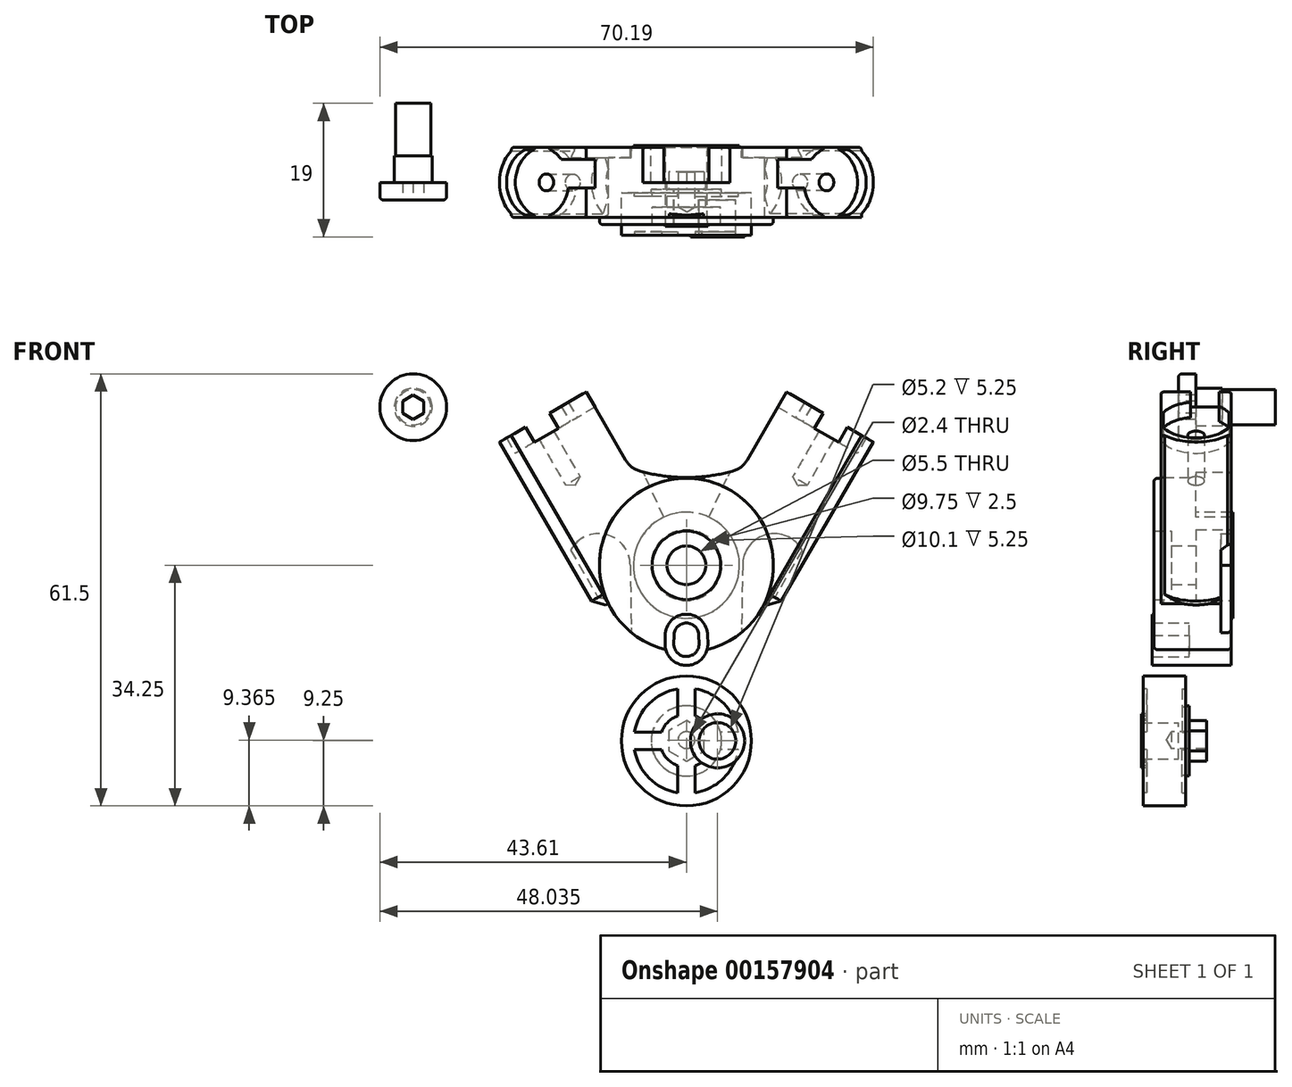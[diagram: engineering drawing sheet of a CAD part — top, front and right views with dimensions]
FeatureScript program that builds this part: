
annotation { "Feature Type Name" : "Feature", "Feature Type Description" : "" }
export const myFeature = defineFeature(function(context is Context, id is Id, definition is map)
    precondition{}
    {
        {
            var Q0;
            Q0=qCreatedBy(makeId("Front.planeOp"),FACE);
            var sketch = newSketch(context, id + "F0", { "sketchPlane" : qUnion([Q0])});
            skPoint(sketch, "E0.orphan", {"position": v(0, -22.5) * mm});
            skLineSegment(sketch, "E1", {"start": v(13, 0) * mm, "end": v(23.68, -6.17) * mm});
            skLineSegment(sketch, "E2.MirrorCS", {"start": v(-13, 0) * mm, "end": v(-23.68, -6.17) * mm});
            skLineSegment(sketch, "E3", {"start": v(-13, 0) * mm, "end": v(-8.66, -7.5) * mm});
            skLineSegment(sketch, "E4", {"start": v(13, 0) * mm, "end": v(8.66, -7.5) * mm});
            skLineSegment(sketch, "E5.MirrorCS", {"start": v(-11.11, -27.95) * mm, "end": v(-23.68, -6.17) * mm});
            skArc(sketch, "E6", {"start": v(-6.55, -9.13) * mm, "mid": v(0, -10) * mm, "end": v(6.55, -9.13) * mm});
            skPoint(sketch, "E7.visualSharp", {"position": v(-7.97, -8.7) * mm});
            skArc(sketch, "E7.filletArc", {"start": v(-8.66, -7.5) * mm, "mid": v(-7.76, -8.52) * mm, "end": v(-6.55, -9.13) * mm});
            skPoint(sketch, "E8.visualSharp", {"position": v(7.97, -8.7) * mm});
            skArc(sketch, "E8.filletArc", {"start": v(6.55, -9.13) * mm, "mid": v(7.76, -8.52) * mm, "end": v(8.66, -7.5) * mm});
            skArc(sketch, "E9", {"start": v(-11.11, -27.95) * mm, "mid": v(0, -34.87) * mm, "end": v(11.11, -27.95) * mm});
            skLineSegment(sketch, "E10", {"start": v(23.68, -6.17) * mm, "end": v(11.11, -27.95) * mm});
            skLineSegment(sketch, "E11", {"start": v(0, -22.5) * mm, "end": v(0, -33.7) * mm});
            skCircle(sketch, "E12", {"center": v(0, -33.7) * mm, "radius": 1.8 * mm});
            skCircle(sketch, "E13.0", {"center": v(0, -33.7) * mm, "radius": 3.05 * mm});
            skSolve(sketch);
        }
        {
            var Q0;
            Q0 = qSketchRegion(id + "F0", true);
            var Q1;
            {var subQ0=sQuery(id+"F0.wireOp",EDGE,"E12");var subQ1=sQuery(id+"F0.wireOp",EDGE,"E9");var subQ2=makeQuery(id+"F0.imprint","INTERSECT",VERTEX,{"disambiguationData":[OD(0.0)],"derivedFrom":[subQ1,subQ0]});Q1=makeQuery(id+"F0.imprint","IMPRINT",FACE,{"disambiguationData":[TD([[makeQuery(id+"F0.imprint","IMPRINT",EDGE,{"disambiguationData":[TD([[subQ2,-1.0]])],"derivedFrom":subQ1}),1.0]])]});}
            var Q2;
            {var subQ0=sQuery(id+"F0.wireOp",EDGE,"E12");var subQ1=sQuery(id+"F0.wireOp",EDGE,"E9");var subQ2=makeQuery(id+"F0.imprint","INTERSECT",VERTEX,{"disambiguationData":[OD(0.0)],"derivedFrom":[subQ1,subQ0]});Q2=makeQuery(id+"F0.imprint","IMPRINT",FACE,{"disambiguationData":[TD([[makeQuery(id+"F0.imprint","IMPRINT",EDGE,{"disambiguationData":[TD([[subQ2,-1.0]])],"derivedFrom":subQ1}),-1.0]])]});}
            extrude(context, id + "F1", {"entities" : qUnion([Q0, Q1, Q2]), "depth" : 10 * mm, "symmetric" : true});
        }
        {
            var Q0;
            Q0=makeQuery(id+"F1.opExtrude","SWEPT_FACE",FACE,{"disambiguationData":[OSD([sQuery(id+"F0.wireOp",EDGE,"E2.MirrorCS")])]});
            var sketch = newSketch(context, id + "F2", { "sketchPlane" : qUnion([Q0])});
            skCircle(sketch, "E14", {"center": v(-19.25, 0) * mm, "radius": 2.06 * mm});
            skSolve(sketch);
        }
        {
            var Q0;
            Q0=makeQuery(id+"F1.opExtrude","SWEPT_FACE",FACE,{"disambiguationData":[OSD([sQuery(id+"F0.wireOp",EDGE,"E1")])]});
            var sketch = newSketch(context, id + "F3", { "sketchPlane" : qUnion([Q0])});
            skPoint(sketch, "E15.orphan", {"position": v(38.32, 0.04) * mm});
            skPoint(sketch, "E16.orphan", {"position": v(-25.5, -0.17) * mm});
            skCircle(sketch, "E17", {"center": v(19.25, 0) * mm, "radius": 1.81 * mm});
            skSolve(sketch);
        }
        {
            var Q0;
            Q0=sQuery(id+"F2.wireOp",VERTEX,"E14.center");
            var Q1;
            Q1=makeQuery(id+"F1.opExtrude","SWEPT_BODY",BODY,{"disambiguationData":[OSD([sQuery(id+"F0.wireOp",EDGE,"rzOBaQMi-jGq5-lYb1-NnJw-oWnWe92DnjdN"),sQuery(id+"F0.wireOp",EDGE,"d8c17911-49cf-4aa5-88f4-c349b0b964bf0.MirrorCS"),sQuery(id+"F0.wireOp",EDGE,"bd97ef09-3599-47c6-b334-9f93c697f875.0"),sQuery(id+"F0.wireOp",EDGE,"KOXjZ0GF-IRyi-H7XW-LbBs-y6uAzEbRzkAs"),sQuery(id+"F0.wireOp",EDGE,"1ec44e12-bc36-4326-98cc-bccb7114c2df.trimOffspring"),sQuery(id+"F0.wireOp",EDGE,"hHBrl5i6-ZnJ3-XNhw-2FA3-8lGi2psnKHFM"),sQuery(id+"F0.wireOp",EDGE,"iY468xlu-Grwu-7jGD-cPJo-sm8Mluo7pk8S"),sQuery(id+"F0.wireOp",EDGE,"xgCmaLVG-ohjl-r4Ya-hG9N-RDTWFdN91myL")])]});
            var Q2;
            Q2=makeQuery(id+"F1.opExtrude","SWEPT_BODY",BODY,{"disambiguationData":[OSD([sQuery(id+"F0.wireOp",EDGE,"rfpI1UyY-z8rJ-t16R-cCYN-fS1l7B0uCpWs"),sQuery(id+"F0.wireOp",EDGE,"E1"),sQuery(id+"F0.wireOp",EDGE,"E2.MirrorCS"),sQuery(id+"F0.wireOp",EDGE,"E3"),sQuery(id+"F0.wireOp",EDGE,"E4"),sQuery(id+"F0.wireOp",EDGE,"lFJJ6whO-Wg9J-KwqN-AuY0-SqxSfbDXyOEt"),sQuery(id+"F0.wireOp",EDGE,"E5.MirrorCS"),sQuery(id+"F0.wireOp",EDGE,"E6"),sQuery(id+"F0.wireOp",EDGE,"E7.filletArc"),sQuery(id+"F0.wireOp",EDGE,"E8.filletArc")])]});
            hole(context, id + "F4", {"style" : HoleStyle.SIMPLE, "endStyle" : HoleEndStyle.BLIND, "standardTappedOrClearance" : lookupTablePath({ "standard" : "ISO", "engagement" : "75%", "pitch" : "0.6 mm", "size" : "M3", "type" : "Tapped" }), "standardBlindInLast" : lookupTablePath({ "standard" : "ISO", "engagement" : "75%", "pitch" : "0.6 mm", "size" : "M3", "type" : "Tapped" }), "holeDiameter" : 2.4 * mm, "holeDepth" : 7.5 * mm, "locations" : qUnion([Q0]), "scope" : qUnion([Q1, Q2]), "startStyle" : HoleStartStyle.SKETCH});
        }
        {
            var Q0;
            Q0=sQuery(id+"F3.wireOp",VERTEX,"E17.center");
            var Q1;
            Q1=makeQuery(id+"F1.opExtrude","SWEPT_BODY",BODY,{"disambiguationData":[OSD([sQuery(id+"F0.wireOp",EDGE,"rfpI1UyY-z8rJ-t16R-cCYN-fS1l7B0uCpWs"),sQuery(id+"F0.wireOp",EDGE,"E1"),sQuery(id+"F0.wireOp",EDGE,"E2.MirrorCS"),sQuery(id+"F0.wireOp",EDGE,"E3"),sQuery(id+"F0.wireOp",EDGE,"E4"),sQuery(id+"F0.wireOp",EDGE,"lFJJ6whO-Wg9J-KwqN-AuY0-SqxSfbDXyOEt"),sQuery(id+"F0.wireOp",EDGE,"E5.MirrorCS"),sQuery(id+"F0.wireOp",EDGE,"E6"),sQuery(id+"F0.wireOp",EDGE,"E7.filletArc"),sQuery(id+"F0.wireOp",EDGE,"E8.filletArc")])]});
            hole(context, id + "F5", {"style" : HoleStyle.SIMPLE, "endStyle" : HoleEndStyle.BLIND, "standardTappedOrClearance" : lookupTablePath({ "standard" : "ISO", "engagement" : "75%", "pitch" : "0.6 mm", "size" : "M3", "type" : "Tapped" }), "standardBlindInLast" : lookupTablePath({ "standard" : "ISO", "engagement" : "75%", "pitch" : "0.6 mm", "size" : "M3", "type" : "Tapped" }), "holeDiameter" : 2.4 * mm, "holeDepth" : 7.5 * mm, "locations" : qUnion([Q0]), "scope" : qUnion([Q1]), "startStyle" : HoleStartStyle.SKETCH});
        }
        {
            var Q0;
            Q0=makeQuery(id+"F1.opExtrude","CAP_FACE",FACE,{"disambiguationData":[OSD([sQuery(id+"F0.wireOp",EDGE,"rfpI1UyY-z8rJ-t16R-cCYN-fS1l7B0uCpWs"),sQuery(id+"F0.wireOp",EDGE,"E1"),sQuery(id+"F0.wireOp",EDGE,"E2.MirrorCS"),sQuery(id+"F0.wireOp",EDGE,"E3"),sQuery(id+"F0.wireOp",EDGE,"E4"),sQuery(id+"F0.wireOp",EDGE,"lFJJ6whO-Wg9J-KwqN-AuY0-SqxSfbDXyOEt"),sQuery(id+"F0.wireOp",EDGE,"E5.MirrorCS"),sQuery(id+"F0.wireOp",EDGE,"E6"),sQuery(id+"F0.wireOp",EDGE,"E7.filletArc"),sQuery(id+"F0.wireOp",EDGE,"E8.filletArc")])],"isStart":false});
            var sketch = newSketch(context, id + "F6", { "sketchPlane" : qUnion([Q0])});
            skCircle(sketch, "E18", {"center": v(0, -22.5) * mm, "radius": 12.37 * mm});
            skCircle(sketch, "E19.0", {"center": v(0, -33.7) * mm, "radius": 3.05 * mm});
            skSolve(sketch);
        }
        {
            var Q0;
            Q0 = qSketchRegion(id + "F6", true);
            extrude(context, id + "F7", {"entities" : qUnion([Q0]), "operationType" : NewBodyOperationType.ADD, "depth" : 1 * mm});
        }
        {
            var Q0;
            Q0=makeQuery(id+"F7.opExtrude","CAP_FACE",FACE,{"disambiguationData":[OSD([sQuery(id+"F6.wireOp",EDGE,"E18")])],"isStart":false});
            var sketch = newSketch(context, id + "F8", { "sketchPlane" : qUnion([Q0])});
            skPoint(sketch, "E20", {"position": v(0, -22.5) * mm});
            skSolve(sketch);
        }
        {
            var Q0;
            Q0=sQuery(id+"F8.wireOp",VERTEX,"E20");
            var Q1;
            Q1=makeQuery(id+"F1.opExtrude","SWEPT_BODY",BODY,{"disambiguationData":[OSD([sQuery(id+"F0.wireOp",EDGE,"rfpI1UyY-z8rJ-t16R-cCYN-fS1l7B0uCpWs"),sQuery(id+"F0.wireOp",EDGE,"E1"),sQuery(id+"F0.wireOp",EDGE,"E2.MirrorCS"),sQuery(id+"F0.wireOp",EDGE,"E3"),sQuery(id+"F0.wireOp",EDGE,"E4"),sQuery(id+"F0.wireOp",EDGE,"lFJJ6whO-Wg9J-KwqN-AuY0-SqxSfbDXyOEt"),sQuery(id+"F0.wireOp",EDGE,"E5.MirrorCS"),sQuery(id+"F0.wireOp",EDGE,"E6"),sQuery(id+"F0.wireOp",EDGE,"E7.filletArc"),sQuery(id+"F0.wireOp",EDGE,"E8.filletArc")])]});
            hole(context, id + "F9", {"style" : HoleStyle.C_BORE, "endStyle" : HoleEndStyle.THROUGH, "holeDiameter" : 5.5 * mm, "cBoreDiameter" : 9.75 * mm, "cBoreDepth" : 2.5 * mm, "locations" : qUnion([Q0]), "scope" : qUnion([Q1]), "isTappedThrough" : true, "startStyle" : HoleStartStyle.SKETCH});
        }
        {
            var Q0;
            Q0=makeQuery(id+"F1.opExtrude","SWEPT_FACE",FACE,{"disambiguationData":[OSD([sQuery(id+"F0.wireOp",EDGE,"E2.MirrorCS")])]});
            var sketch = newSketch(context, id + "F10", { "sketchPlane" : qUnion([Q0])});
            skLineSegment(sketch, "E21.0", {"start": v(-23.6, -4.5) * mm, "end": v(-23.6, 4.5) * mm});
            skArc(sketch, "E22", {"start": v(-23.6, 4.5) * mm, "mid": v(-25.5, 0) * mm, "end": v(-23.6, -4.5) * mm});
            skPoint(sketch, "E23.orphan", {"position": v(-23.6, -5) * mm});
            skPoint(sketch, "E24.orphan", {"position": v(-23.6, 5) * mm});
            skSolve(sketch);
        }
        {
            var Q0;
            Q0=makeQuery(id+"FtnkNii1LFd0vET_1.boolean.opBoolean","MERGE",FACE,{"derivedFrom":[makeQuery(id+"F1.opExtrude","SWEPT_FACE",FACE,{"disambiguationData":[OSD([sQuery(id+"F0.wireOp",EDGE,"E2.MirrorCS")])]}),makeQuery(id+"FtnkNii1LFd0vET_1.opSweep","CAP_FACE",FACE,{"disambiguationData":[OSD([sQuery(id+"F0.wireOp",VERTEX,"E5.MirrorCS.end"),sQuery(id+"F10.wireOp",EDGE,"03euvT1h-kaf3-RjWf-RbOj-bPACf7aRniEZ"),sQuery(id+"F10.wireOp",EDGE,"Vvxw1KTZ-P8wy-A8oR-Xbjp-Nn9TtI1LRVrt")])],"isStart":true})]});
            var sketch = newSketch(context, id + "F11", { "sketchPlane" : qUnion([Q0])});
            skArc(sketch, "E25", {"start": v(-15.36, 3.3) * mm, "mid": v(-16.22, 4.1) * mm, "end": v(-17.25, 4.7) * mm});
            skLineSegment(sketch, "E26", {"start": v(-23.6, 5) * mm, "end": v(-21.25, 5) * mm});
            skLineSegment(sketch, "E27", {"start": v(-11.25, 5) * mm, "end": v(-11.25, 3.3) * mm});
            skLineSegment(sketch, "E28", {"start": v(-11.25, -5) * mm, "end": v(-17.25, -5) * mm});
            skLineSegment(sketch, "E29", {"start": v(-11.25, 3.3) * mm, "end": v(-15.36, 3.3) * mm});
            skLineSegment(sketch, "E30", {"start": v(-11.25, -0.8) * mm, "end": v(-14.21, -0.8) * mm});
            skLineSegment(sketch, "E31.trimOffspring", {"start": v(-11.25, -0.8) * mm, "end": v(-11.25, -5) * mm});
            skLineSegment(sketch, "E32", {"start": v(-23.6, 5) * mm, "end": v(-23.6, 4.5) * mm});
            skLineSegment(sketch, "E33.trimOffspring", {"start": v(-23.6, -4.5) * mm, "end": v(-23.6, -5) * mm});
            skArc(sketch, "E34.trimOffspring", {"start": v(-21.25, 4.7) * mm, "mid": v(-24.35, 0) * mm, "end": v(-21.25, -4.7) * mm});
            skArc(sketch, "E35.trimOffspring", {"start": v(-17.25, -4.7) * mm, "mid": v(-15.23, -3.14) * mm, "end": v(-14.21, -0.8) * mm});
            skLineSegment(sketch, "E36", {"start": v(-21.25, 5) * mm, "end": v(-21.25, 4.7) * mm});
            skLineSegment(sketch, "E37.0", {"start": v(-17.25, 5) * mm, "end": v(-17.25, 4.7) * mm});
            skLineSegment(sketch, "E38.trimOffspring", {"start": v(-17.25, 5) * mm, "end": v(-11.25, 5) * mm});
            skLineSegment(sketch, "E39.trimOffspring", {"start": v(-17.25, -4.7) * mm, "end": v(-17.25, -5) * mm});
            skLineSegment(sketch, "E40.trimOffspring", {"start": v(-18.25, -5) * mm, "end": v(-20.25, -5) * mm});
            skLineSegment(sketch, "E41.trimOffspring", {"start": v(-21.25, -5) * mm, "end": v(-23.6, -5) * mm});
            skLineSegment(sketch, "E42.trimOffspring", {"start": v(-21.25, -4.7) * mm, "end": v(-21.25, -5) * mm});
            skArc(sketch, "E43", {"start": v(-23.6, 4.5) * mm, "mid": v(-25.5, 0) * mm, "end": v(-23.6, -4.5) * mm});
            skSolve(sketch);
        }
        {
            var Q0;
            Q0 = qSketchRegion(id + "F11", true);
            extrude(context, id + "F12", {"entities" : qUnion([Q0]), "operationType" : NewBodyOperationType.ADD, "depth" : 2.5 * mm});
        }
        {
            var Q0;
            Q0=makeQuery(id+"FtnkNii1LFd0vET_1.boolean.opBoolean","MERGE",FACE,{"derivedFrom":[makeQuery(id+"F1.opExtrude","SWEPT_FACE",FACE,{"disambiguationData":[OSD([sQuery(id+"F0.wireOp",EDGE,"E1")])]}),makeQuery(id+"FtnkNii1LFd0vET_1.opSweep","CAP_FACE",FACE,{"disambiguationData":[OSD([sQuery(id+"F0.wireOp",VERTEX,"lFJJ6whO-Wg9J-KwqN-AuY0-SqxSfbDXyOEt.end"),sQuery(id+"F10.wireOp",EDGE,"03euvT1h-kaf3-RjWf-RbOj-bPACf7aRniEZ"),sQuery(id+"F10.wireOp",EDGE,"Vvxw1KTZ-P8wy-A8oR-Xbjp-Nn9TtI1LRVrt")])],"isStart":false})]});
            var sketch = newSketch(context, id + "F13", { "sketchPlane" : qUnion([Q0])});
            skArc(sketch, "E44", {"start": v(14.21, -0.8) * mm, "mid": v(15.23, -3.14) * mm, "end": v(17.25, -4.7) * mm});
            skLineSegment(sketch, "E45", {"start": v(11.25, -5) * mm, "end": v(11.25, -0.8) * mm});
            skLineSegment(sketch, "E46", {"start": v(11.25, 5) * mm, "end": v(17.25, 5) * mm});
            skLineSegment(sketch, "E47", {"start": v(11.25, -5) * mm, "end": v(17.25, -5) * mm});
            skLineSegment(sketch, "E48", {"start": v(11.25, 3.3) * mm, "end": v(15.36, 3.3) * mm});
            skLineSegment(sketch, "E49", {"start": v(11.25, -0.8) * mm, "end": v(14.21, -0.8) * mm});
            skLineSegment(sketch, "E50.trimOffspring", {"start": v(11.25, 3.3) * mm, "end": v(11.25, 5) * mm});
            skArc(sketch, "E51", {"start": v(23.6, -4.5) * mm, "mid": v(25.5, 0) * mm, "end": v(23.6, 4.5) * mm});
            skLineSegment(sketch, "E52", {"start": v(21.25, -5) * mm, "end": v(21.25, -4.7) * mm});
            skLineSegment(sketch, "E53.0", {"start": v(17.25, -5) * mm, "end": v(17.25, -4.7) * mm});
            skLineSegment(sketch, "E54.trimOffspring", {"start": v(21.25, 4.7) * mm, "end": v(21.25, 5) * mm});
            skLineSegment(sketch, "E55.trimOffspring", {"start": v(17.25, 4.7) * mm, "end": v(17.25, 5) * mm});
            skArc(sketch, "E56.trimOffspring", {"start": v(17.25, 4.7) * mm, "mid": v(16.22, 4.1) * mm, "end": v(15.36, 3.3) * mm});
            skArc(sketch, "E57.trimOffspring", {"start": v(21.25, -4.7) * mm, "mid": v(24.35, 0) * mm, "end": v(21.25, 4.7) * mm});
            skLineSegment(sketch, "E58", {"start": v(21.25, 5) * mm, "end": v(23.6, 5) * mm});
            skLineSegment(sketch, "E59", {"start": v(21.25, -5) * mm, "end": v(23.6, -5) * mm});
            skLineSegment(sketch, "E60", {"start": v(23.6, -5) * mm, "end": v(23.6, -4.5) * mm});
            skLineSegment(sketch, "E61", {"start": v(23.6, 4.5) * mm, "end": v(23.6, 5) * mm});
            skSolve(sketch);
        }
        {
            var Q0;
            Q0 = qSketchRegion(id + "F13", true);
            extrude(context, id + "F14", {"entities" : qUnion([Q0]), "operationType" : NewBodyOperationType.ADD, "depth" : 2.5 * mm});
        }
        {
            var Q0;
            Q0=makeQuery(id+"F10.imprint","IMPRINT",FACE,{"disambiguationData":[TD([[makeQuery(id+"F10.imprint","IMPRINT",EDGE,{"derivedFrom":sQuery(id+"F10.wireOp",EDGE,"E21.0")}),1.0]])]});
            var Q1;
            Q1=sQuery(id+"F0.wireOp",EDGE,"E5.MirrorCS");
            sweep(context, id + "F15", {"operationType" : NewBodyOperationType.ADD, "profiles" : qUnion([Q0]), "path" : qUnion([Q1])});
        }
        {
            var Q0;
            Q0=makeQuery(id+"F14.opExtrude","CAP_FACE",FACE,{"disambiguationData":[OSD([sQuery(id+"F13.wireOp",EDGE,"SZVnfSIk-eu6L-TS2M-XrId-ek2R4wEcxdL5"),sQuery(id+"F13.wireOp",EDGE,"E51"),sQuery(id+"F13.wireOp",EDGE,"d2ed7b6c-8a1b-4353-8f4a-99a53af964f0.trimOffspring"),sQuery(id+"F13.wireOp",EDGE,"E52"),sQuery(id+"F13.wireOp",EDGE,"E54.trimOffspring"),sQuery(id+"F13.wireOp",EDGE,"3468f3f2-538a-47e8-9c80-37b50e91f819.trimOffspring"),sQuery(id+"F13.wireOp",EDGE,"E57.trimOffspring"),sQuery(id+"F13.wireOp",EDGE,"c19fe44b-0edd-49b7-be39-237bb749a952.trimOffspring")])],"isStart":true});
            var sketch = newSketch(context, id + "F16", { "sketchPlane" : qUnion([Q0])});
            skArc(sketch, "E62.0", {"start": v(23.6, 4.5) * mm, "mid": v(25.5, 0) * mm, "end": v(23.6, -4.5) * mm});
            skLineSegment(sketch, "E63", {"start": v(23.6, 4.5) * mm, "end": v(23.6, -4.5) * mm});
            skSolve(sketch);
        }
        {
            var Q0;
            Q0 = qSketchRegion(id + "F16", true);
            var Q1;
            Q1=sQuery(id+"F0.wireOp",EDGE,"E10");
            sweep(context, id + "F17", {"operationType" : NewBodyOperationType.ADD, "profiles" : qUnion([Q0]), "path" : qUnion([Q1])});
        }
        {
            var Q0;
            Q0=makeQuery(id+"F14.boolean.opBoolean","MERGE",FACE,{"derivedFrom":[makeQuery(id+"F12.boolean.opBoolean","MERGE",FACE,{"derivedFrom":[makeQuery(id+"F1.opExtrude","CAP_FACE",FACE,{"disambiguationData":[OSD([sQuery(id+"F0.wireOp",EDGE,"rfpI1UyY-z8rJ-t16R-cCYN-fS1l7B0uCpWs"),sQuery(id+"F0.wireOp",EDGE,"E1"),sQuery(id+"F0.wireOp",EDGE,"E2.MirrorCS"),sQuery(id+"F0.wireOp",EDGE,"E3"),sQuery(id+"F0.wireOp",EDGE,"E4"),sQuery(id+"F0.wireOp",EDGE,"lFJJ6whO-Wg9J-KwqN-AuY0-SqxSfbDXyOEt"),sQuery(id+"F0.wireOp",EDGE,"E5.MirrorCS"),sQuery(id+"F0.wireOp",EDGE,"E6"),sQuery(id+"F0.wireOp",EDGE,"E7.filletArc"),sQuery(id+"F0.wireOp",EDGE,"E8.filletArc"),sQuery(id+"F0.wireOp",EDGE,"Z6kVz02L-fb5r-uzOL-jqxl-xZ710giCbPzr")])],"isStart":true}),makeQuery(id+"F12.opExtrude","SWEPT_FACE",FACE,{"disambiguationData":[OSD([sQuery(id+"F11.wireOp",EDGE,"E26")])]})]}),makeQuery(id+"F14.opExtrude","SWEPT_FACE",FACE,{"disambiguationData":[OSD([sQuery(id+"F13.wireOp",EDGE,"E46")])]})]});
            var sketch = newSketch(context, id + "F18", { "sketchPlane" : qUnion([Q0])});
            skCircle(sketch, "E64", {"center": v(0, -22.5) * mm, "radius": 5.05 * mm});
            skSolve(sketch);
        }
        {
            var Q0;
            Q0 = qSketchRegion(id + "F18", true);
            extrude(context, id + "F19", {"entities" : qUnion([Q0]), "operationType" : NewBodyOperationType.REMOVE, "oppositeDirection" : true, "depth" : 5 * mm});
        }
        {
            var Q0;
            Q0=makeQuery(id+"F15.opSweep","CAP_EDGE",EDGE,{"disambiguationData":[OSD([sQuery(id+"F0.wireOp",VERTEX,"E5.MirrorCS.start"),sQuery(id+"F10.wireOp",EDGE,"E22")])],"isStart":false});
            var Q1;
            Q1=makeQuery(id+"F17.opSweep","CAP_EDGE",EDGE,{"disambiguationData":[OSD([sQuery(id+"F0.wireOp",VERTEX,"E10.end"),sQuery(id+"F16.wireOp",EDGE,"E62.0")])],"isStart":false});
            chamfer(context, id + "F20", {"entities" : qUnion([Q0, Q1]), "width" : 1.5 * mm, "tangentPropagation" : true});
        }
        {
            var Q0;
            Q0=qCreatedBy(makeId("Front.planeOp"),FACE);
            cPlane(context, id + "F21", {"entities" : qUnion([Q0]), "cplaneType" : CPlaneType.OFFSET, "offset" : 1.5 * mm, "width" : 150 * mm, "height" : 150 * mm});
        }
        {
            var Q0;
            Q0=qCreatedBy(id+"F21.planeOp",FACE);
            var sketch = newSketch(context, id + "F22", { "sketchPlane" : qUnion([Q0])});
            skCircle(sketch, "E65", {"center": v(0, -47.5) * mm, "radius": 9.25 * mm});
            skSolve(sketch);
        }
        {
            var Q0;
            Q0 = qSketchRegion(id + "F22", true);
            extrude(context, id + "F23", {"entities" : qUnion([Q0]), "depth" : 6 * mm});
        }
        {
            var Q0;
            Q0=makeQuery(id+"F23.opExtrude","CAP_FACE",FACE,{"disambiguationData":[OSD([sQuery(id+"F22.wireOp",EDGE,"E65")])],"isStart":false});
            var sketch = newSketch(context, id + "F24", { "sketchPlane" : qUnion([Q0])});
            skCircle(sketch, "E66", {"center": v(0, -47.5) * mm, "radius": 4.42 * mm});
            skCircle(sketch, "E67", {"center": v(4.42, -47.5) * mm, "radius": 2.6 * mm});
            skCircle(sketch, "E68.0", {"center": v(4.42, -47.5) * mm, "radius": 3.85 * mm});
            skLineSegment(sketch, "E69", {"start": v(4.42, -47.5) * mm, "end": v(0, -47.5) * mm});
            skSolve(sketch);
        }
        {
            var Q0;
            {var subQ0=sQuery(id+"F24.wireOp",EDGE,"E67");var subQ1=sQuery(id+"F24.wireOp",EDGE,"E66");var subQ2=makeQuery(id+"F24.imprint","INTERSECT",VERTEX,{"disambiguationData":[OD(0.0)],"derivedFrom":[subQ1,subQ0]});Q0=makeQuery(id+"F24.imprint","IMPRINT",FACE,{"disambiguationData":[TD([[makeQuery(id+"F24.imprint","IMPRINT",EDGE,{"disambiguationData":[TD([[subQ2,-1.0]])],"derivedFrom":subQ1}),1.0]])]});}
            var Q1;
            {var subQ0=sQuery(id+"F24.wireOp",EDGE,"E67");var subQ1=sQuery(id+"F24.wireOp",EDGE,"E66");var subQ2=makeQuery(id+"F24.imprint","INTERSECT",VERTEX,{"disambiguationData":[OD(0.0)],"derivedFrom":[subQ1,subQ0]});Q1=makeQuery(id+"F24.imprint","IMPRINT",FACE,{"disambiguationData":[TD([[makeQuery(id+"F24.imprint","IMPRINT",EDGE,{"disambiguationData":[TD([[subQ2,-1.0]])],"derivedFrom":subQ1}),-1.0]])]});}
            var Q2;
            {var subQ0=sQuery(id+"F24.wireOp",EDGE,"E68.0");var subQ1=sQuery(id+"F24.wireOp",EDGE,"E66");var subQ2=makeQuery(id+"F24.imprint","INTERSECT",VERTEX,{"disambiguationData":[OD(1.0)],"derivedFrom":[subQ1,subQ0]});Q2=makeQuery(id+"F24.imprint","IMPRINT",FACE,{"disambiguationData":[TD([[makeQuery(id+"F24.imprint","IMPRINT",EDGE,{"disambiguationData":[TD([[subQ2,-1.0]])],"derivedFrom":subQ1}),-1.0]])]});}
            var Q3;
            {var subQ0=sQuery(id+"F24.wireOp",EDGE,"E68.0");var subQ1=sQuery(id+"F24.wireOp",EDGE,"E66");var subQ2=makeQuery(id+"F24.imprint","INTERSECT",VERTEX,{"disambiguationData":[OD(1.0)],"derivedFrom":[subQ1,subQ0]});Q3=makeQuery(id+"F24.imprint","IMPRINT",FACE,{"disambiguationData":[TD([[makeQuery(id+"F24.imprint","IMPRINT",EDGE,{"disambiguationData":[TD([[subQ2,-1.0]])],"derivedFrom":subQ1}),1.0]])]});}
            extrude(context, id + "F25", {"entities" : qUnion([Q0, Q1, Q2, Q3]), "operationType" : NewBodyOperationType.ADD, "depth" : 0.25 * mm});
        }
        {
            var Q0;
            Q0=makeQuery(id+"F25.boolean.opBoolean","SPLIT",FACE,{"disambiguationData":[TD([makeQuery(id+"F25.opExtrude","SWEPT_FACE",FACE,{"disambiguationData":[OSD([sQuery(id+"F24.wireOp",EDGE,"E67")])]})])],"derivedFrom":makeQuery(id+"F23.opExtrude","CAP_FACE",FACE,{"disambiguationData":[OSD([sQuery(id+"F22.wireOp",EDGE,"E65")])],"isStart":false})});
            extrude(context, id + "F26", {"entities" : qUnion([Q0]), "operationType" : NewBodyOperationType.REMOVE, "oppositeDirection" : true, "depth" : 5 * mm});
        }
        {
            var Q0;
            Q0=makeQuery(id+"F23.opExtrude","CAP_FACE",FACE,{"disambiguationData":[OSD([sQuery(id+"F22.wireOp",EDGE,"E65")])],"isStart":true});
            var sketch = newSketch(context, id + "F27", { "sketchPlane" : qUnion([Q0])});
            skArc(sketch, "E70", {"start": v(-1.25, -42.66) * mm, "mid": v(-3.54, -43.96) * mm, "end": v(-4.84, -46.25) * mm});
            skArc(sketch, "E71", {"start": v(-1.25, -40.1) * mm, "mid": v(-5.3, -42.2) * mm, "end": v(-7.4, -46.25) * mm});
            skLineSegment(sketch, "E72.left", {"start": v(-1.25, -40.1) * mm, "end": v(-1.25, -42.66) * mm});
            skLineSegment(sketch, "E72.right", {"start": v(1.25, -40.1) * mm, "end": v(1.25, -42.66) * mm});
            skLineSegment(sketch, "E73.bottom", {"start": v(-7.4, -46.25) * mm, "end": v(-4.84, -46.25) * mm});
            skLineSegment(sketch, "E73.top", {"start": v(-7.4, -48.75) * mm, "end": v(-4.84, -48.75) * mm});
            skLineSegment(sketch, "E74.trimOffspring", {"start": v(4.84, -46.25) * mm, "end": v(7.4, -46.25) * mm});
            skLineSegment(sketch, "E75.trimOffspring", {"start": v(4.84, -48.75) * mm, "end": v(7.4, -48.75) * mm});
            skArc(sketch, "E76.trimOffspring", {"start": v(4.84, -46.25) * mm, "mid": v(3.54, -43.96) * mm, "end": v(1.25, -42.66) * mm});
            skArc(sketch, "E77.trimOffspring", {"start": v(7.4, -46.25) * mm, "mid": v(5.3, -42.2) * mm, "end": v(1.25, -40.1) * mm});
            skArc(sketch, "E78.trimOffspring", {"start": v(-7.4, -48.75) * mm, "mid": v(-5.3, -52.8) * mm, "end": v(-1.25, -54.9) * mm});
            skArc(sketch, "E79.trimOffspring", {"start": v(1.25, -54.9) * mm, "mid": v(5.3, -52.8) * mm, "end": v(7.4, -48.75) * mm});
            skArc(sketch, "E80", {"start": v(1.25, -52.34) * mm, "mid": v(3.54, -51.04) * mm, "end": v(4.84, -48.75) * mm});
            skLineSegment(sketch, "E81", {"start": v(-1.25, -54.9) * mm, "end": v(-1.25, -52.34) * mm});
            skLineSegment(sketch, "E82", {"start": v(1.25, -54.9) * mm, "end": v(1.25, -52.34) * mm});
            skArc(sketch, "E83.trimOffspring", {"start": v(-4.84, -48.75) * mm, "mid": v(-3.54, -51.04) * mm, "end": v(-1.25, -52.34) * mm});
            skSolve(sketch);
        }
        {
            var Q0;
            Q0 = qSketchRegion(id + "F27", true);
            extrude(context, id + "F28", {"entities" : qUnion([Q0]), "operationType" : NewBodyOperationType.REMOVE, "oppositeDirection" : true, "depth" : 0.5 * mm});
        }
        {
            var Q0;
            {var subQ0=sQuery(id+"F22.wireOp",EDGE,"E65");Q0=makeQuery(id+"FpMMcBae6gBmIsD_2.boolean.opBoolean","MERGE",FACE,{"derivedFrom":[makeQuery(id+"F25.boolean.opBoolean","SPLIT",FACE,{"disambiguationData":[TD([makeQuery(id+"F23.opExtrude","SWEPT_FACE",FACE,{"disambiguationData":[OSD([subQ0])]})])],"derivedFrom":makeQuery(id+"F23.opExtrude","CAP_FACE",FACE,{"disambiguationData":[OSD([subQ0])],"isStart":false})}),makeQuery(id+"FpMMcBae6gBmIsD_2.opExtrude","CAP_FACE",FACE,{"disambiguationData":[OSD([sQuery(id+"FuiqfWvG5TbSWox_2.wireOp",EDGE,"G7TCtbeU-HK3a-Q5oG-1v0c-rmRTOBJ5wWQV")])],"isStart":true})]});}
            var sketch = newSketch(context, id + "F29", { "sketchPlane" : qUnion([Q0])});
            skArc(sketch, "E84", {"start": v(-3.54, -48.74) * mm, "mid": v(-2.65, -50.15) * mm, "end": v(-1.25, -51.03) * mm});
            skLineSegment(sketch, "E85", {"start": v(-1.25, -40.1) * mm, "end": v(-1.25, -43.96) * mm});
            skLineSegment(sketch, "E86.MirrorCS", {"start": v(1.25, -40.1) * mm, "end": v(1.25, -43.96) * mm});
            skLineSegment(sketch, "E87.MirrorCS", {"start": v(-1.25, -54.89) * mm, "end": v(-1.25, -51.03) * mm});
            skLineSegment(sketch, "E88.MirrorCS", {"start": v(1.25, -54.89) * mm, "end": v(1.25, -51.03) * mm});
            skLineSegment(sketch, "E89", {"start": v(-3.54, -46.24) * mm, "end": v(-7.4, -46.24) * mm});
            skLineSegment(sketch, "E90.MirrorCS", {"start": v(-3.54, -48.74) * mm, "end": v(-7.4, -48.74) * mm});
            skArc(sketch, "E91.trimOffspring", {"start": v(-1.25, -43.96) * mm, "mid": v(-2.65, -44.84) * mm, "end": v(-3.54, -46.24) * mm});
            skArc(sketch, "E92.trimOffspring", {"start": v(-1.25, -40.1) * mm, "mid": v(-5.3, -42.2) * mm, "end": v(-7.4, -46.24) * mm});
            skArc(sketch, "E93.trimOffspring", {"start": v(1.25, -51.03) * mm, "mid": v(1.72, -50.83) * mm, "end": v(2.15, -50.56) * mm});
            skArc(sketch, "E94.trimOffspring", {"start": v(2.16, -44.43) * mm, "mid": v(1.72, -44.16) * mm, "end": v(1.25, -43.96) * mm});
            skArc(sketch, "E95", {"start": v(6.93, -44.63) * mm, "mid": v(4.58, -43.7) * mm, "end": v(2.16, -44.43) * mm});
            skArc(sketch, "E96", {"start": v(-7.4, -48.74) * mm, "mid": v(-5.3, -52.8) * mm, "end": v(-1.25, -54.89) * mm});
            skArc(sketch, "E97.trimOffspring", {"start": v(1.25, -54.89) * mm, "mid": v(4.67, -53.37) * mm, "end": v(6.92, -50.38) * mm});
            skArc(sketch, "E98.trimOffspring", {"start": v(6.93, -44.63) * mm, "mid": v(4.67, -41.63) * mm, "end": v(1.25, -40.1) * mm});
            skArc(sketch, "E99.trimOffspring", {"start": v(2.15, -50.56) * mm, "mid": v(4.57, -51.31) * mm, "end": v(6.92, -50.38) * mm});
            skSolve(sketch);
        }
        {
            var Q0;
            Q0 = qSketchRegion(id + "F29", true);
            extrude(context, id + "F30", {"entities" : qUnion([Q0]), "operationType" : NewBodyOperationType.REMOVE, "oppositeDirection" : true, "depth" : 0.5 * mm});
        }
        {
            var Q0;
            Q0=makeQuery(id+"F14.boolean.opBoolean","MERGE",FACE,{"derivedFrom":[makeQuery(id+"F12.boolean.opBoolean","MERGE",FACE,{"derivedFrom":[makeQuery(id+"F1.opExtrude","CAP_FACE",FACE,{"disambiguationData":[OSD([sQuery(id+"F0.wireOp",EDGE,"E1"),sQuery(id+"F0.wireOp",EDGE,"E2.MirrorCS"),sQuery(id+"F0.wireOp",EDGE,"E3"),sQuery(id+"F0.wireOp",EDGE,"E4"),sQuery(id+"F0.wireOp",EDGE,"lFJJ6whO-Wg9J-KwqN-AuY0-SqxSfbDXyOEt"),sQuery(id+"F0.wireOp",EDGE,"E5.MirrorCS"),sQuery(id+"F0.wireOp",EDGE,"E6"),sQuery(id+"F0.wireOp",EDGE,"E7.filletArc"),sQuery(id+"F0.wireOp",EDGE,"E8.filletArc"),sQuery(id+"F0.wireOp",EDGE,"WRP7mDvc-YLdO-b3qg-z12u-TlJDe7pmeXIB"),sQuery(id+"F0.wireOp",EDGE,"RhdyVmHK-tO6j-kY6Q-7TJN-yxXFlVGlmahh")])],"isStart":true}),makeQuery(id+"F12.opExtrude","SWEPT_FACE",FACE,{"disambiguationData":[OSD([sQuery(id+"F11.wireOp",EDGE,"E26")])]}),makeQuery(id+"F12.opExtrude","SWEPT_FACE",FACE,{"disambiguationData":[OSD([sQuery(id+"F11.wireOp",EDGE,"E38.trimOffspring")])]})]}),makeQuery(id+"F14.opExtrude","SWEPT_FACE",FACE,{"disambiguationData":[OSD([sQuery(id+"F13.wireOp",EDGE,"E46")])]}),makeQuery(id+"F14.opExtrude","SWEPT_FACE",FACE,{"disambiguationData":[OSD([sQuery(id+"F13.wireOp",EDGE,"3468f3f2-538a-47e8-9c80-37b50e91f819.trimOffspring")])]})]});
            var sketch = newSketch(context, id + "F31", { "sketchPlane" : qUnion([Q0])});
            skCircle(sketch, "E100.0", {"center": v(0, -22.5) * mm, "radius": 5.05 * mm});
            skCircle(sketch, "E101.0", {"center": v(0, -22.5) * mm, "radius": 7.55 * mm});
            skSolve(sketch);
        }
        {
            var Q0;
            Q0 = qSketchRegion(id + "F31", true);
            extrude(context, id + "F32", {"entities" : qUnion([Q0]), "operationType" : NewBodyOperationType.ADD, "depth" : 0.25 * mm});
        }
        {
            var Q0;
            Q0=makeQuery(id+"F7.opExtrude","CAP_EDGE",EDGE,{"disambiguationData":[OSD([sQuery(id+"F6.wireOp",EDGE,"bee525e0-0782-45c0-85c4-5cf85354ca50.trimOffspring")])],"isStart":false});
            var Q1;
            Q1=makeQuery(id+"F14.boolean.opBoolean","MERGE",EDGE,{"derivedFrom":[makeQuery(id+"F1.opExtrude","CAP_EDGE",EDGE,{"disambiguationData":[OSD([sQuery(id+"F0.wireOp",EDGE,"lFJJ6whO-Wg9J-KwqN-AuY0-SqxSfbDXyOEt")])],"isStart":false}),makeQuery(id+"F14.opExtrude","SWEPT_EDGE",EDGE,{"disambiguationData":[OSD([sQuery(id+"F13.wireOp",EDGE,"SZVnfSIk-eu6L-TS2M-XrId-ek2R4wEcxdL5"),sQuery(id+"F13.wireOp",EDGE,"c19fe44b-0edd-49b7-be39-237bb749a952.trimOffspring")])]})]});
            var Q2;
            Q2=makeQuery(id+"F12.boolean.opBoolean","MERGE",EDGE,{"derivedFrom":[makeQuery(id+"F1.opExtrude","CAP_EDGE",EDGE,{"disambiguationData":[OSD([sQuery(id+"F0.wireOp",EDGE,"E5.MirrorCS")])],"isStart":false}),makeQuery(id+"F12.opExtrude","SWEPT_EDGE",EDGE,{"disambiguationData":[OSD([sQuery(id+"F11.wireOp",EDGE,"E33.trimOffspring"),sQuery(id+"F11.wireOp",EDGE,"E41.trimOffspring")])]})]});
            var Q3;
            Q3=makeQuery(id+"F12.boolean.opBoolean","MERGE",EDGE,{"derivedFrom":[makeQuery(id+"F1.opExtrude","CAP_EDGE",EDGE,{"disambiguationData":[OSD([sQuery(id+"F0.wireOp",EDGE,"E3")])],"isStart":false}),makeQuery(id+"F12.opExtrude","SWEPT_EDGE",EDGE,{"disambiguationData":[OSD([sQuery(id+"F11.wireOp",EDGE,"E28"),sQuery(id+"F11.wireOp",EDGE,"E31.trimOffspring")])]})]});
            var Q4;
            Q4=makeQuery(id+"F14.boolean.opBoolean","MERGE",EDGE,{"derivedFrom":[makeQuery(id+"F1.opExtrude","CAP_EDGE",EDGE,{"disambiguationData":[OSD([sQuery(id+"F0.wireOp",EDGE,"E4")])],"isStart":true}),makeQuery(id+"F14.opExtrude","SWEPT_EDGE",EDGE,{"disambiguationData":[OSD([sQuery(id+"F13.wireOp",EDGE,"E46"),sQuery(id+"F13.wireOp",EDGE,"E50.trimOffspring")])]})]});
            var Q5;
            Q5=makeQuery(id+"F12.boolean.opBoolean","MERGE",EDGE,{"derivedFrom":[makeQuery(id+"F1.opExtrude","CAP_EDGE",EDGE,{"disambiguationData":[OSD([sQuery(id+"F0.wireOp",EDGE,"E3")])],"isStart":true}),makeQuery(id+"F12.opExtrude","SWEPT_EDGE",EDGE,{"disambiguationData":[OSD([sQuery(id+"F11.wireOp",EDGE,"E27"),sQuery(id+"F11.wireOp",EDGE,"E38.trimOffspring")])]})]});
            var Q6;
            Q6=makeQuery(id+"F12.boolean.opBoolean","MERGE",EDGE,{"derivedFrom":[makeQuery(id+"F1.opExtrude","CAP_EDGE",EDGE,{"disambiguationData":[OSD([sQuery(id+"F0.wireOp",EDGE,"E5.MirrorCS")])],"isStart":true}),makeQuery(id+"F12.opExtrude","SWEPT_EDGE",EDGE,{"disambiguationData":[OSD([sQuery(id+"F11.wireOp",EDGE,"E26"),sQuery(id+"F11.wireOp",EDGE,"E32")])]})]});
            var Q7;
            Q7=makeQuery(id+"F14.boolean.opBoolean","MERGE",EDGE,{"derivedFrom":[makeQuery(id+"F1.opExtrude","CAP_EDGE",EDGE,{"disambiguationData":[OSD([sQuery(id+"F0.wireOp",EDGE,"lFJJ6whO-Wg9J-KwqN-AuY0-SqxSfbDXyOEt")])],"isStart":true}),makeQuery(id+"F14.opExtrude","SWEPT_EDGE",EDGE,{"disambiguationData":[OSD([sQuery(id+"F13.wireOp",EDGE,"d2ed7b6c-8a1b-4353-8f4a-99a53af964f0.trimOffspring"),sQuery(id+"F13.wireOp",EDGE,"3468f3f2-538a-47e8-9c80-37b50e91f819.trimOffspring")])]})]});
            var Q8;
            Q8=makeQuery(id+"F1.opExtrude","CAP_EDGE",EDGE,{"disambiguationData":[OSD([sQuery(id+"F0.wireOp",EDGE,"RhdyVmHK-tO6j-kY6Q-7TJN-yxXFlVGlmahh")])],"isStart":true});
            var Q9;
            Q9=makeQuery(id+"F1.opExtrude","CAP_EDGE",EDGE,{"disambiguationData":[OSD([sQuery(id+"F0.wireOp",EDGE,"WRP7mDvc-YLdO-b3qg-z12u-TlJDe7pmeXIB")])],"isStart":true});
            var Q10;
            Q10=makeQuery(id+"F7.opExtrude","CAP_EDGE",EDGE,{"disambiguationData":[OSD([sQuery(id+"F6.wireOp",EDGE,"E18")])],"isStart":false});
            var Q11;
            Q11=makeQuery(id+"F1.opExtrude","CAP_EDGE",EDGE,{"disambiguationData":[OSD([sQuery(id+"F0.wireOp",EDGE,"E9")])],"isStart":true});
            fillet(context, id + "F33", {"entities" : qUnion([Q0, Q1, Q2, Q3, Q4, Q5, Q6, Q7, Q8, Q9, Q10, Q11]), "radius" : 0.5 * mm, "tangentPropagation" : true, "allowEdgeOverflow" : false});
        }
        {
            var Q0;
            Q0=makeQuery(id+"F23.opExtrude","CAP_FACE",FACE,{"disambiguationData":[OSD([sQuery(id+"F22.wireOp",EDGE,"E65")])],"isStart":true});
            var sketch = newSketch(context, id + "F34", { "sketchPlane" : qUnion([Q0])});
            skCircle(sketch, "E102", {"center": v(0, -47.5) * mm, "radius": 5 * mm});
            skSolve(sketch);
        }
        {
            var Q0;
            Q0 = qSketchRegion(id + "F34", true);
            extrude(context, id + "F35", {"entities" : qUnion([Q0]), "operationType" : NewBodyOperationType.ADD, "depth" : 0.5 * mm});
        }
        {
            var Q0;
            Q0=makeQuery(id+"F35.opExtrude","CAP_FACE",FACE,{"disambiguationData":[OSD([sQuery(id+"F34.wireOp",EDGE,"E102")])],"isStart":false});
            var sketch = newSketch(context, id + "F36", { "sketchPlane" : qUnion([Q0])});
            skCircle(sketch, "E103.cCircle", {"center": v(0, -47.5) * mm, "radius": 2.5 * mm, "construction": true});
            skLineSegment(sketch, "E103.0", {"start": v(2.5, -46.06) * mm, "end": v(2.5, -48.94) * mm});
            skLineSegment(sketch, "E103.1", {"start": v(2.5, -48.94) * mm, "end": v(0, -50.39) * mm});
            skLineSegment(sketch, "E103.2", {"start": v(0, -50.39) * mm, "end": v(-2.5, -48.94) * mm});
            skLineSegment(sketch, "E103.3", {"start": v(-2.5, -48.94) * mm, "end": v(-2.5, -46.06) * mm});
            skLineSegment(sketch, "E103.4", {"start": v(-2.5, -46.06) * mm, "end": v(0, -44.61) * mm});
            skLineSegment(sketch, "E103.5", {"start": v(0, -44.61) * mm, "end": v(2.5, -46.06) * mm});
            skSolve(sketch);
        }
        {
            var Q0;
            Q0 = qSketchRegion(id + "F36", true);
            extrude(context, id + "F37", {"entities" : qUnion([Q0]), "operationType" : NewBodyOperationType.ADD, "depth" : 2.5 * mm});
        }
        {
            var Q0;
            Q0=makeQuery(id+"F37.opExtrude","CAP_FACE",FACE,{"disambiguationData":[OSD([sQuery(id+"F36.wireOp",EDGE,"E103.0"),sQuery(id+"F36.wireOp",EDGE,"E103.1"),sQuery(id+"F36.wireOp",EDGE,"E103.2"),sQuery(id+"F36.wireOp",EDGE,"E103.3"),sQuery(id+"F36.wireOp",EDGE,"E103.4"),sQuery(id+"F36.wireOp",EDGE,"E103.5")])],"isStart":false});
            var sketch = newSketch(context, id + "F38", { "sketchPlane" : qUnion([Q0])});
            skCircle(sketch, "E104", {"center": v(0, -47.39) * mm, "radius": 0.9 * mm});
            skSolve(sketch);
        }
        {
            var Q0;
            Q0=sQuery(id+"F38.wireOp",VERTEX,"E104.center");
            var Q1;
            Q1=makeQuery(id+"F23.opExtrude","SWEPT_BODY",BODY,{"disambiguationData":[OSD([sQuery(id+"F22.wireOp",EDGE,"E65")])]});
            hole(context, id + "F39", {"style" : HoleStyle.SIMPLE, "endStyle" : HoleEndStyle.BLIND, "standardTappedOrClearance" : lookupTablePath({ "standard" : "ISO", "engagement" : "75%", "pitch" : "0.6 mm", "size" : "M3", "type" : "Tapped" }), "standardBlindInLast" : lookupTablePath({ "standard" : "ISO", "engagement" : "75%", "pitch" : "0.6 mm", "size" : "M3", "type" : "Tapped" }), "holeDiameter" : 2.4 * mm, "holeDepth" : 5 * mm, "locations" : qUnion([Q0]), "scope" : qUnion([Q1]), "startStyle" : HoleStartStyle.SKETCH});
        }
        {
            var Q0;
            Q0=makeQuery(id+"F7.opExtrude","CAP_FACE",FACE,{"disambiguationData":[OSD([sQuery(id+"F6.wireOp",EDGE,"E18")])],"isStart":false});
            var sketch = newSketch(context, id + "F40", { "sketchPlane" : qUnion([Q0])});
            skPoint(sketch, "E105.start.orphan", {"position": v(0, -22.5) * mm});
            skPoint(sketch, "E106.start.orphan", {"position": v(0, -32.5) * mm});
            skArc(sketch, "E107", {"start": v(1.77, -32.5) * mm, "mid": v(0, -30.72) * mm, "end": v(-1.78, -32.5) * mm});
            skArc(sketch, "E108.0", {"start": v(-1.8, -33.66) * mm, "mid": v(0, -35.5) * mm, "end": v(1.8, -33.66) * mm});
            skArc(sketch, "E109.0", {"start": v(3.03, -32.5) * mm, "mid": v(0, -29.47) * mm, "end": v(-3.03, -32.5) * mm});
            skArc(sketch, "E110.0", {"start": v(-3.05, -33.64) * mm, "mid": v(0, -36.75) * mm, "end": v(3.05, -33.63) * mm});
            skLineSegment(sketch, "E111", {"start": v(-3.03, -32.5) * mm, "end": v(-3.05, -33.64) * mm});
            skLineSegment(sketch, "E112", {"start": v(3.03, -32.5) * mm, "end": v(3.05, -33.63) * mm});
            skLineSegment(sketch, "E113", {"start": v(1.77, -32.5) * mm, "end": v(1.8, -33.66) * mm});
            skLineSegment(sketch, "E114", {"start": v(-1.78, -32.5) * mm, "end": v(-1.8, -33.66) * mm});
            skSolve(sketch);
        }
        {
            var Q0;
            Q0 = qSketchRegion(id + "F40", true);
            extrude(context, id + "F41", {"entities" : qUnion([Q0]), "operationType" : NewBodyOperationType.ADD, "depth" : 0.25 * mm});
        }
        {
            var Q0;
            Q0=makeQuery(id+"F41.boolean.opBoolean","SPLIT",FACE,{"disambiguationData":[TD([makeQuery(id+"F41.opExtrude","SWEPT_FACE",FACE,{"disambiguationData":[OSD([sQuery(id+"F40.wireOp",EDGE,"E107")])]})])],"derivedFrom":makeQuery(id+"F7.opExtrude","CAP_FACE",FACE,{"disambiguationData":[OSD([sQuery(id+"F6.wireOp",EDGE,"E18"),sQuery(id+"F6.wireOp",EDGE,"E19.0")])],"isStart":false})});
            extrude(context, id + "F42", {"entities" : qUnion([Q0]), "operationType" : NewBodyOperationType.REMOVE, "oppositeDirection" : true, "depth" : 5 * mm});
        }
        {
            var Q0;
            Q0=qCreatedBy(makeId("Front.planeOp"),FACE);
            var sketch = newSketch(context, id + "F43", { "sketchPlane" : qUnion([Q0])});
            skCircle(sketch, "E115", {"center": v(-38.86, 0) * mm, "radius": 4.75 * mm});
            skSolve(sketch);
        }
        {
            var Q0;
            Q0 = qSketchRegion(id + "F43", true);
            extrude(context, id + "F44", {"entities" : qUnion([Q0]), "depth" : 2.5 * mm});
        }
        {
            var Q0;
            Q0=makeQuery(id+"F44.opExtrude","CAP_FACE",FACE,{"disambiguationData":[OSD([sQuery(id+"F43.wireOp",EDGE,"E115")])],"isStart":true});
            var sketch = newSketch(context, id + "F45", { "sketchPlane" : qUnion([Q0])});
            skCircle(sketch, "E116", {"center": v(38.86, 0) * mm, "radius": 2.7 * mm});
            skSolve(sketch);
        }
        {
            var Q0;
            Q0 = qSketchRegion(id + "F45", true);
            extrude(context, id + "F46", {"entities" : qUnion([Q0]), "operationType" : NewBodyOperationType.ADD, "depth" : 3.75 * mm});
        }
        {
            var Q0;
            Q0=makeQuery(id+"F46.opExtrude","CAP_FACE",FACE,{"disambiguationData":[OSD([sQuery(id+"F45.wireOp",EDGE,"E116")])],"isStart":false});
            var sketch = newSketch(context, id + "F47", { "sketchPlane" : qUnion([Q0])});
            skCircle(sketch, "E117", {"center": v(38.86, 0) * mm, "radius": 2.5 * mm});
            skSolve(sketch);
        }
        {
            var Q0;
            Q0 = qSketchRegion(id + "F47", true);
            extrude(context, id + "F48", {"entities" : qUnion([Q0]), "operationType" : NewBodyOperationType.ADD, "depth" : 7.5 * mm});
        }
        {
            var Q0;
            Q0=makeQuery(id+"F44.opExtrude","CAP_FACE",FACE,{"disambiguationData":[OSD([sQuery(id+"F43.wireOp",EDGE,"E115")])],"isStart":false});
            var sketch = newSketch(context, id + "F49", { "sketchPlane" : qUnion([Q0])});
            skPoint(sketch, "E118", {"position": v(-38.86, 0) * mm});
            skCircle(sketch, "E119.cCircle", {"center": v(-38.86, 0) * mm, "radius": 1.5 * mm, "construction": true});
            skLineSegment(sketch, "E119.0", {"start": v(-37.36, 0.87) * mm, "end": v(-37.36, -0.87) * mm});
            skLineSegment(sketch, "E119.1", {"start": v(-37.36, -0.87) * mm, "end": v(-38.86, -1.73) * mm});
            skLineSegment(sketch, "E119.2", {"start": v(-38.86, -1.73) * mm, "end": v(-40.36, -0.87) * mm});
            skLineSegment(sketch, "E119.3", {"start": v(-40.36, -0.87) * mm, "end": v(-40.36, 0.87) * mm});
            skLineSegment(sketch, "E119.4", {"start": v(-40.36, 0.87) * mm, "end": v(-38.86, 1.73) * mm});
            skLineSegment(sketch, "E119.5", {"start": v(-38.86, 1.73) * mm, "end": v(-37.36, 0.87) * mm});
            skPoint(sketch, "E119.0.midPoint", {"position": v(-37.36, 0) * mm});
            skSolve(sketch);
        }
        {
            var Q0;
            Q0 = qSketchRegion(id + "F49", true);
            extrude(context, id + "F50", {"entities" : qUnion([Q0]), "operationType" : NewBodyOperationType.REMOVE, "oppositeDirection" : true, "depth" : 2.5 * mm});
        }
        {
            var Q0;
            Q0=makeQuery(id+"F44.opExtrude","CAP_EDGE",EDGE,{"disambiguationData":[OSD([sQuery(id+"F43.wireOp",EDGE,"E115")])],"isStart":false});
            var Q1;
            Q1=makeQuery(id+"F50.boolean.opBoolean","COPY",EDGE,{"derivedFrom":makeQuery(id+"F50.opExtrude","CAP_EDGE",EDGE,{"disambiguationData":[OSD([sQuery(id+"F49.wireOp",EDGE,"E119.5")])],"isStart":true})});
            var Q2;
            Q2=makeQuery(id+"F50.boolean.opBoolean","COPY",EDGE,{"derivedFrom":makeQuery(id+"F50.opExtrude","CAP_EDGE",EDGE,{"disambiguationData":[OSD([sQuery(id+"F49.wireOp",EDGE,"E119.4")])],"isStart":true})});
            var Q3;
            Q3=makeQuery(id+"F50.boolean.opBoolean","COPY",EDGE,{"derivedFrom":makeQuery(id+"F50.opExtrude","CAP_EDGE",EDGE,{"disambiguationData":[OSD([sQuery(id+"F49.wireOp",EDGE,"E119.3")])],"isStart":true})});
            var Q4;
            Q4=makeQuery(id+"F50.boolean.opBoolean","COPY",EDGE,{"derivedFrom":makeQuery(id+"F50.opExtrude","CAP_EDGE",EDGE,{"disambiguationData":[OSD([sQuery(id+"F49.wireOp",EDGE,"E119.2")])],"isStart":true})});
            var Q5;
            Q5=makeQuery(id+"F50.boolean.opBoolean","COPY",EDGE,{"derivedFrom":makeQuery(id+"F50.opExtrude","CAP_EDGE",EDGE,{"disambiguationData":[OSD([sQuery(id+"F49.wireOp",EDGE,"E119.1")])],"isStart":true})});
            var Q6;
            Q6=makeQuery(id+"F50.boolean.opBoolean","COPY",EDGE,{"derivedFrom":makeQuery(id+"F50.opExtrude","CAP_EDGE",EDGE,{"disambiguationData":[OSD([sQuery(id+"F49.wireOp",EDGE,"E119.0")])],"isStart":true})});
            fillet(context, id + "F51", {"entities" : qUnion([Q0, Q1, Q2, Q3, Q4, Q5, Q6]), "radius" : 0.5 * mm, "tangentPropagation" : true, "allowEdgeOverflow" : false});
        }
        {
            var Q0;
            Q0=qCreatedBy(makeId("Front.planeOp"),FACE);
            var sketch = newSketch(context, id + "F52", { "sketchPlane" : qUnion([Q0])});
            skArc(sketch, "E120.0", {"start": v(3.2, -15.66) * mm, "mid": v(0, -14.95) * mm, "end": v(-3.2, -15.66) * mm});
            skLineSegment(sketch, "E121", {"start": v(-3.2, -15.66) * mm, "end": v(-6.7, -8.14) * mm});
            skLineSegment(sketch, "E122.MirrorCS", {"start": v(3.2, -15.66) * mm, "end": v(6.7, -8.14) * mm});
            skPoint(sketch, "E123.start.orphan", {"position": v(0, -14.95) * mm});
            skArc(sketch, "E124", {"start": v(6.7, -8.14) * mm, "mid": v(0, -6.66) * mm, "end": v(-6.7, -8.14) * mm});
            skSolve(sketch);
        }
        {
            var Q0;
            Q0 = qSketchRegion(id + "F52", true);
            extrude(context, id + "F53", {"entities" : qUnion([Q0]), "operationType" : NewBodyOperationType.REMOVE, "endBound" : BoundingType.THROUGH_ALL, "oppositeDirection" : true, "depth" : 25 * mm});
        }
        {
            var Q0;
            Q0=makeQuery(id+"F14.boolean.opBoolean","MERGE",FACE,{"derivedFrom":[makeQuery(id+"F12.boolean.opBoolean","MERGE",FACE,{"derivedFrom":[makeQuery(id+"F1.opExtrude","CAP_FACE",FACE,{"disambiguationData":[OSD([sQuery(id+"F0.wireOp",EDGE,"E1"),sQuery(id+"F0.wireOp",EDGE,"E2.MirrorCS"),sQuery(id+"F0.wireOp",EDGE,"E3"),sQuery(id+"F0.wireOp",EDGE,"E4"),sQuery(id+"F0.wireOp",EDGE,"E5.MirrorCS"),sQuery(id+"F0.wireOp",EDGE,"E6"),sQuery(id+"F0.wireOp",EDGE,"E7.filletArc"),sQuery(id+"F0.wireOp",EDGE,"E8.filletArc"),sQuery(id+"F0.wireOp",EDGE,"E9"),sQuery(id+"F0.wireOp",EDGE,"E10"),sQuery(id+"F0.wireOp",EDGE,"E13.0")])],"isStart":true}),makeQuery(id+"F12.opExtrude","SWEPT_FACE",FACE,{"disambiguationData":[OSD([sQuery(id+"F11.wireOp",EDGE,"E26")])]}),makeQuery(id+"F12.opExtrude","SWEPT_FACE",FACE,{"disambiguationData":[OSD([sQuery(id+"F11.wireOp",EDGE,"E38.trimOffspring")])]})]}),makeQuery(id+"F14.opExtrude","SWEPT_FACE",FACE,{"disambiguationData":[OSD([sQuery(id+"F13.wireOp",EDGE,"E46")])]}),makeQuery(id+"F14.opExtrude","SWEPT_FACE",FACE,{"disambiguationData":[OSD([sQuery(id+"F13.wireOp",EDGE,"E58")])]})]});
            var sketch = newSketch(context, id + "F54", { "sketchPlane" : qUnion([Q0])});
            skArc(sketch, "E125.0", {"start": v(7.83, -32.08) * mm, "mid": v(7.81, -32.1) * mm, "end": v(7.8, -32.11) * mm});
            skPoint(sketch, "E126.orphan", {"position": v(-24.93, -4) * mm});
            skPoint(sketch, "E127.orphan", {"position": v(24.93, -4) * mm});
            skArc(sketch, "E128", {"start": v(16.87, -23.56) * mm, "mid": v(13.03, -18.03) * mm, "end": v(8, -22.5) * mm});
            skLineSegment(sketch, "E129", {"start": v(8, -22.5) * mm, "end": v(7.8, -34.16) * mm});
            skLineSegment(sketch, "E130", {"start": v(7.8, -34.16) * mm, "end": v(13.41, -34.26) * mm});
            skLineSegment(sketch, "E131", {"start": v(13.41, -34.26) * mm, "end": v(16.87, -23.56) * mm});
            skLineSegment(sketch, "E132.MirrorCS", {"start": v(-8, -22.5) * mm, "end": v(-7.8, -34.16) * mm});
            skArc(sketch, "E133.MirrorCS", {"start": v(-16.87, -23.56) * mm, "mid": v(-13.03, -18.03) * mm, "end": v(-8, -22.5) * mm});
            skLineSegment(sketch, "E134.MirrorCS", {"start": v(-13.41, -34.26) * mm, "end": v(-16.87, -23.56) * mm});
            skLineSegment(sketch, "E135.MirrorCS", {"start": v(-7.8, -34.16) * mm, "end": v(-13.41, -34.26) * mm});
            skSolve(sketch);
        }
        {
            var Q0;
            Q0 = qSketchRegion(id + "F54", true);
            extrude(context, id + "F55", {"entities" : qUnion([Q0]), "operationType" : NewBodyOperationType.REMOVE, "oppositeDirection" : true, "depth" : 1.5 * mm});
        }
    });
